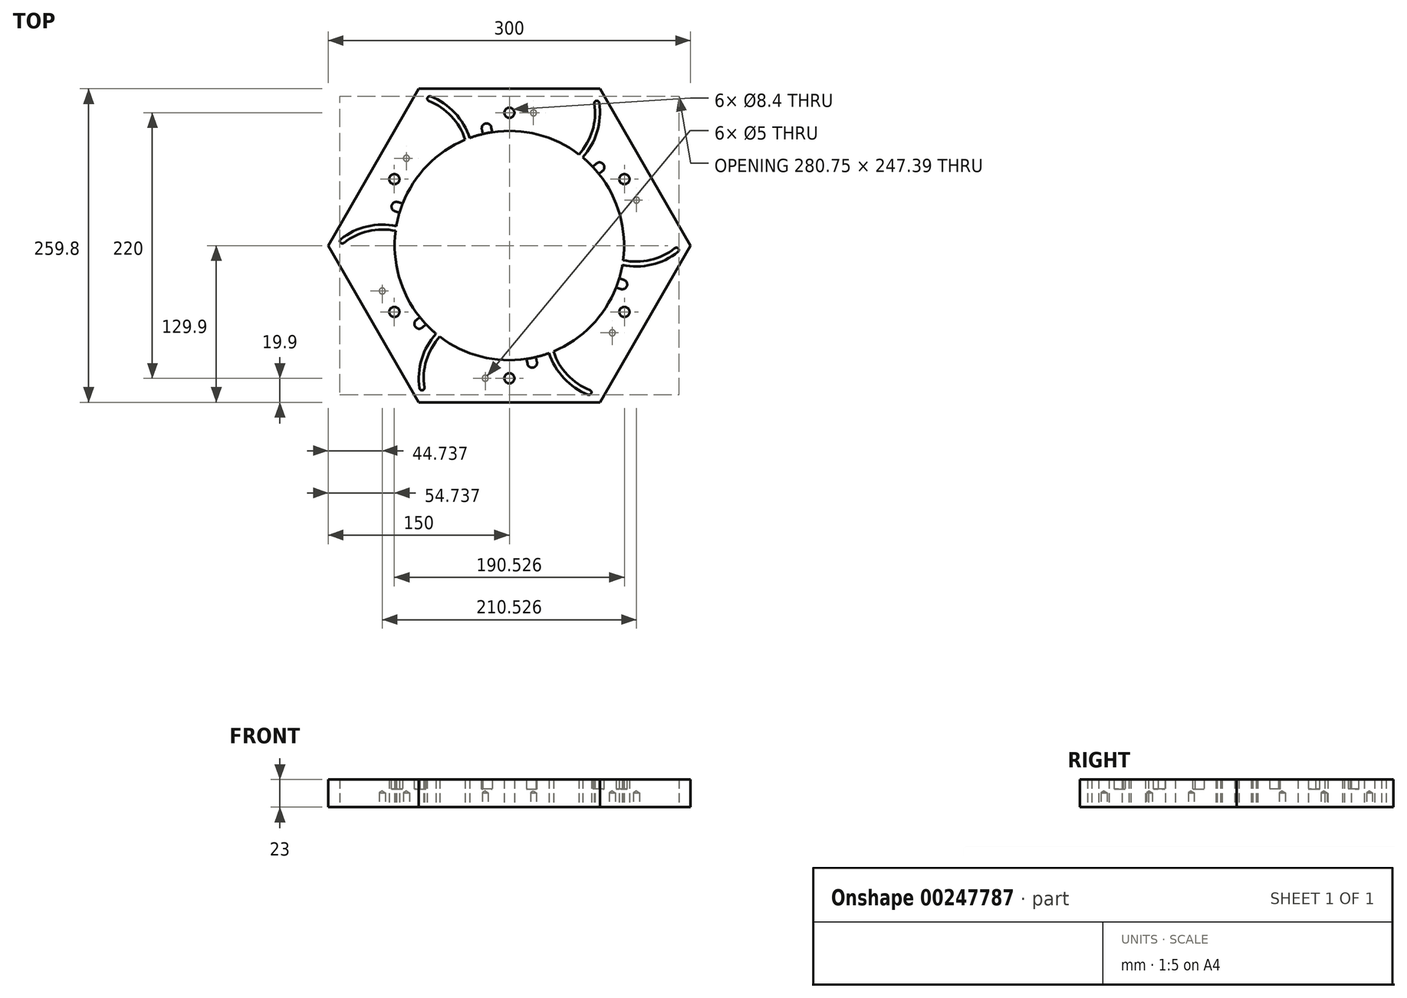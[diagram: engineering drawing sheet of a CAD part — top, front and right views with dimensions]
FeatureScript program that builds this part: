
annotation { "Feature Type Name" : "Feature", "Feature Type Description" : "" }
export const myFeature = defineFeature(function(context is Context, id is Id, definition is map)
    precondition{}
    {
        {
            var Q0;
            Q0=qCreatedBy(makeId("Top.planeOp"),FACE);
            var sketch = newSketch(context, id + "F0", { "sketchPlane" : qUnion([Q0])});
            skCircle(sketch, "E0.cCircle", {"center": v(0, 0) * mm, "radius": 150 * mm, "construction": true});
            skLineSegment(sketch, "E0.0", {"start": v(-75, 129.9) * mm, "end": v(75, 129.9) * mm});
            skLineSegment(sketch, "E0.1", {"start": v(75, 129.9) * mm, "end": v(150, 0) * mm});
            skLineSegment(sketch, "E0.2", {"start": v(150, 0) * mm, "end": v(75, -129.9) * mm});
            skLineSegment(sketch, "E0.3", {"start": v(75, -129.9) * mm, "end": v(-75, -129.9) * mm});
            skLineSegment(sketch, "E0.4", {"start": v(-75, -129.9) * mm, "end": v(-150, 0) * mm});
            skLineSegment(sketch, "E0.5", {"start": v(-150, 0) * mm, "end": v(-75, 129.9) * mm});
            skCircle(sketch, "E1", {"center": v(0, 0) * mm, "radius": 95 * mm});
            skCircle(sketch, "E2", {"center": v(0, 0) * mm, "radius": 110 * mm, "construction": true});
            skCircle(sketch, "E3", {"center": v(0, 110) * mm, "radius": 4.2 * mm});
            skCircle(sketch, "E4.1.0", {"center": v(-95.26, 55) * mm, "radius": 4.2 * mm});
            skCircle(sketch, "E4.2.0", {"center": v(-95.26, -55) * mm, "radius": 4.2 * mm});
            skCircle(sketch, "E4.3.0", {"center": v(0, -110) * mm, "radius": 4.2 * mm});
            skCircle(sketch, "E4.4.0", {"center": v(95.26, -55) * mm, "radius": 4.2 * mm});
            skCircle(sketch, "E4.5.0", {"center": v(95.26, 55) * mm, "radius": 4.2 * mm});
            skSolve(sketch);
        }
        {
            var Q0;
            Q0=qCreatedBy(makeId("Front.planeOp"),FACE);
            var sketch = newSketch(context, id + "F1", { "sketchPlane" : qUnion([Q0])});
            skLineSegment(sketch, "E5", {"start": v(0, -93.36) * mm, "end": v(0, 93) * mm, "construction": true});
            skSolve(sketch);
        }
        {
            var Q0;
            Q0=makeQuery(id+"F0.imprint","IMPRINT",FACE,{"disambiguationData":[TD([[makeQuery(id+"F0.imprint","IMPRINT",EDGE,{"derivedFrom":sQuery(id+"F0.wireOp",EDGE,"E0.0")}),-1.0]])]});
            extrude(context, id + "F2", {"entities" : qUnion([Q0]), "depth" : 25 * mm, "hasSecondDirection" : true, "secondDirectionOppositeDirection" : false, "secondDirectionDepth" : 2 * mm});
        }
        {
            var Q0;
            Q0=qCreatedBy(makeId("Top.planeOp"),FACE);
            var sketch = newSketch(context, id + "F3", { "sketchPlane" : qUnion([Q0])});
            skArc(sketch, "E6.0", {"start": v(-30.7, 79.26) * mm, "mid": v(-41.9, 106.16) * mm, "end": v(-65.27, 123.56) * mm});
            skArc(sketch, "E7.0", {"start": v(-34.54, 77.66) * mm, "mid": v(-44.72, 103.26) * mm, "end": v(-66.72, 119.83) * mm});
            skArc(sketch, "E8.0", {"start": v(-67.73, 122.7) * mm, "mid": v(-67.88, 121.03) * mm, "end": v(-66.72, 119.83) * mm});
            skArc(sketch, "E9.0", {"start": v(-65.27, 123.56) * mm, "mid": v(-66.66, 123.58) * mm, "end": v(-67.73, 122.7) * mm});
            skArc(sketch, "E10.0", {"start": v(-30.7, 79.26) * mm, "mid": v(-32.63, 78.49) * mm, "end": v(-34.54, 77.66) * mm});
            skSolve(sketch);
        }
        {
            var Q0;
            Q0=qSketchRegion(id+"F3",true);
            extrude(context, id + "F4", {"entities" : qUnion([Q0]), "depth" : 35 * mm, "hasSecondDirection" : true, "secondDirectionOppositeDirection" : true, "secondDirectionDepth" : 10 * mm});
        }
        {
            var Q0;
            Q0=makeQuery(id+"F4.opExtrude","SWEPT_BODY",BODY,{"disambiguationData":[OSD([sQuery(id+"F3.wireOp",EDGE,"E6.0"),sQuery(id+"F3.wireOp",EDGE,"E7.0"),sQuery(id+"F3.wireOp",EDGE,"E8.0"),sQuery(id+"F3.wireOp",EDGE,"E9.0"),sQuery(id+"F3.wireOp",EDGE,"E10.0")])]});
            var Q1;
            Q1=sQuery(id+"F1.wireOp",EDGE,"E5");
            circularPattern(context, id + "F5", {"entities" : qUnion([Q0]), "axis" : qUnion([Q1]), "angle" : 360 * degree, "instanceCount" : 6, "equalSpace" : true});
        }
        {
            var Q0;
            Q0=makeQuery(id+"F4.opExtrude","SWEPT_BODY",BODY,{"disambiguationData":[OSD([sQuery(id+"F3.wireOp",EDGE,"E6.0"),sQuery(id+"F3.wireOp",EDGE,"E7.0"),sQuery(id+"F3.wireOp",EDGE,"E8.0"),sQuery(id+"F3.wireOp",EDGE,"E9.0"),sQuery(id+"F3.wireOp",EDGE,"E10.0")])]});
            var Q1;
            Q1=makeQuery(id+"F5.opPattern","COPY",BODY,{"derivedFrom":makeQuery(id+"F4.opExtrude","SWEPT_BODY",BODY,{"disambiguationData":[OSD([sQuery(id+"F3.wireOp",EDGE,"E6.0"),sQuery(id+"F3.wireOp",EDGE,"E7.0"),sQuery(id+"F3.wireOp",EDGE,"E8.0"),sQuery(id+"F3.wireOp",EDGE,"E9.0"),sQuery(id+"F3.wireOp",EDGE,"E10.0")])]}),"instanceName":"5"});
            var Q2;
            Q2=makeQuery(id+"F5.opPattern","COPY",BODY,{"derivedFrom":makeQuery(id+"F4.opExtrude","SWEPT_BODY",BODY,{"disambiguationData":[OSD([sQuery(id+"F3.wireOp",EDGE,"E6.0"),sQuery(id+"F3.wireOp",EDGE,"E7.0"),sQuery(id+"F3.wireOp",EDGE,"E8.0"),sQuery(id+"F3.wireOp",EDGE,"E9.0"),sQuery(id+"F3.wireOp",EDGE,"E10.0")])]}),"instanceName":"4"});
            var Q3;
            Q3=makeQuery(id+"F5.opPattern","COPY",BODY,{"derivedFrom":makeQuery(id+"F4.opExtrude","SWEPT_BODY",BODY,{"disambiguationData":[OSD([sQuery(id+"F3.wireOp",EDGE,"E6.0"),sQuery(id+"F3.wireOp",EDGE,"E7.0"),sQuery(id+"F3.wireOp",EDGE,"E8.0"),sQuery(id+"F3.wireOp",EDGE,"E9.0"),sQuery(id+"F3.wireOp",EDGE,"E10.0")])]}),"instanceName":"3"});
            var Q4;
            Q4=makeQuery(id+"F5.opPattern","COPY",BODY,{"derivedFrom":makeQuery(id+"F4.opExtrude","SWEPT_BODY",BODY,{"disambiguationData":[OSD([sQuery(id+"F3.wireOp",EDGE,"E6.0"),sQuery(id+"F3.wireOp",EDGE,"E7.0"),sQuery(id+"F3.wireOp",EDGE,"E8.0"),sQuery(id+"F3.wireOp",EDGE,"E9.0"),sQuery(id+"F3.wireOp",EDGE,"E10.0")])]}),"instanceName":"2"});
            var Q5;
            Q5=makeQuery(id+"F5.opPattern","COPY",BODY,{"derivedFrom":makeQuery(id+"F4.opExtrude","SWEPT_BODY",BODY,{"disambiguationData":[OSD([sQuery(id+"F3.wireOp",EDGE,"E6.0"),sQuery(id+"F3.wireOp",EDGE,"E7.0"),sQuery(id+"F3.wireOp",EDGE,"E8.0"),sQuery(id+"F3.wireOp",EDGE,"E9.0"),sQuery(id+"F3.wireOp",EDGE,"E10.0")])]}),"instanceName":"1"});
            var Q6;
            Q6=makeQuery(id+"F2.opExtrude","SWEPT_BODY",BODY,{"disambiguationData":[OSD([sQuery(id+"F0.wireOp",EDGE,"E0.0"),sQuery(id+"F0.wireOp",EDGE,"E0.1"),sQuery(id+"F0.wireOp",EDGE,"E0.2"),sQuery(id+"F0.wireOp",EDGE,"E0.3"),sQuery(id+"F0.wireOp",EDGE,"E0.4"),sQuery(id+"F0.wireOp",EDGE,"E0.5"),sQuery(id+"F0.wireOp",EDGE,"E1")])]});
            booleanBodies(context, id + "F6", {"operationType" : BooleanOperationType.SUBTRACTION, "tools" : qUnion([Q0, Q1, Q2, Q3, Q4, Q5]), "targets" : qUnion([Q6])});
        }
        {
            var Q0;
            Q0=makeQuery(id+"F2.opExtrude","CAP_FACE",FACE,{"disambiguationData":[OSD([sQuery(id+"F0.wireOp",EDGE,"E0.0"),sQuery(id+"F0.wireOp",EDGE,"E0.1"),sQuery(id+"F0.wireOp",EDGE,"E0.2"),sQuery(id+"F0.wireOp",EDGE,"E0.3"),sQuery(id+"F0.wireOp",EDGE,"E0.4"),sQuery(id+"F0.wireOp",EDGE,"E0.5"),sQuery(id+"F0.wireOp",EDGE,"E1")])],"isStart":false});
            var sketch = newSketch(context, id + "F7", { "sketchPlane" : qUnion([Q0])});
            skCircle(sketch, "E11", {"center": v(0, 0) * mm, "radius": 95 * mm, "construction": true});
            skCircle(sketch, "E12", {"center": v(0, 0) * mm, "radius": 99 * mm, "construction": true});
            skLineSegment(sketch, "E13", {"start": v(0, 0) * mm, "end": v(0, 115.62) * mm, "construction": true});
            skLineSegment(sketch, "E14", {"start": v(0, 0) * mm, "end": v(-23.06, 118.63) * mm, "construction": true});
            skPoint(sketch, "E15", {"position": v(-18.9, 97.18) * mm});
            skArc(sketch, "E16", {"start": v(-19.65, 101.1) * mm, "mid": v(-22.23, 99.38) * mm, "end": v(-22.8, 96.34) * mm});
            skLineSegment(sketch, "E17", {"start": v(-22.82, 96.42) * mm, "end": v(-20.7, 85.51) * mm});
            skLineSegment(sketch, "E18", {"start": v(-16.77, 86.28) * mm, "end": v(-20.7, 85.51) * mm});
            skArc(sketch, "E19.MirrorCS", {"start": v(-19.65, 101.1) * mm, "mid": v(-16.62, 100.47) * mm, "end": v(-14.95, 97.86) * mm});
            skLineSegment(sketch, "E20.MirrorCS", {"start": v(-16.77, 86.28) * mm, "end": v(-12.84, 87.04) * mm});
            skLineSegment(sketch, "E21.MirrorCS", {"start": v(-14.96, 97.94) * mm, "end": v(-12.84, 87.04) * mm});
            skSolve(sketch);
        }
        {
            var Q0;
            Q0=qSketchRegion(id+"F7",true);
            extrude(context, id + "F8", {"entities" : qUnion([Q0]), "oppositeDirection" : true, "depth" : 8 * mm, "hasSecondDirection" : true, "secondDirectionOppositeDirection" : false, "secondDirectionDepth" : 10 * mm});
        }
        {
            var Q0;
            Q0=makeQuery(id+"F8.opExtrude","SWEPT_BODY",BODY,{"disambiguationData":[OSD([sQuery(id+"F7.wireOp",EDGE,"E16"),sQuery(id+"F7.wireOp",EDGE,"E17"),sQuery(id+"F7.wireOp",EDGE,"E18"),sQuery(id+"F7.wireOp",EDGE,"E19.MirrorCS"),sQuery(id+"F7.wireOp",EDGE,"E20.MirrorCS"),sQuery(id+"F7.wireOp",EDGE,"E21.MirrorCS")])]});
            var Q1;
            Q1=sQuery(id+"F1.wireOp",EDGE,"E5");
            circularPattern(context, id + "F9", {"operationType" : NewBodyOperationType.REMOVE, "entities" : qUnion([Q0]), "axis" : qUnion([Q1]), "angle" : 360 * degree, "instanceCount" : 6, "equalSpace" : true});
        }
        {
            var Q0;
            Q0=makeQuery(id+"F0.imprint","IMPRINT",FACE,{"disambiguationData":[TD([[makeQuery(id+"F0.imprint","IMPRINT",EDGE,{"derivedFrom":sQuery(id+"F0.wireOp",EDGE,"E0.0")}),-1.0]])]});
            cPlane(context, id + "F10", {"entities" : qUnion([Q0]), "cplaneType" : CPlaneType.OFFSET, "offset" : 0 * mm, "width" : 150 * mm, "height" : 150 * mm});
        }
        {
            var Q0;
            Q0=qCreatedBy(id+"F10.planeOp",FACE);
            var sketch = newSketch(context, id + "F11", { "sketchPlane" : qUnion([Q0])});
            skPoint(sketch, "E22.0", {"position": v(-85.26, 72.32) * mm});
            skPoint(sketch, "E23.1.0", {"position": v(-105.26, -37.68) * mm});
            skPoint(sketch, "E23.2.0", {"position": v(-20, -110) * mm});
            skPoint(sketch, "E23.3.0", {"position": v(85.26, -72.32) * mm});
            skPoint(sketch, "E23.4.0", {"position": v(105.26, 37.68) * mm});
            skPoint(sketch, "E23.5.0", {"position": v(20, 110) * mm});
            skPoint(sketch, "E23.center", {"position": v(0, 0) * mm});
            skSolve(sketch);
        }
        {
            var Q0;
            Q0=sQuery(id+"F11.wireOp",VERTEX,"E22.0");
            var Q1;
            Q1=sQuery(id+"F11.wireOp",VERTEX,"E23.5.0");
            var Q2;
            Q2=sQuery(id+"F11.wireOp",VERTEX,"E23.4.0");
            var Q3;
            Q3=sQuery(id+"F11.wireOp",VERTEX,"E23.3.0");
            var Q4;
            Q4=sQuery(id+"F11.wireOp",VERTEX,"E23.2.0");
            var Q5;
            Q5=sQuery(id+"F11.wireOp",VERTEX,"E23.1.0");
            var Q6;
            Q6=makeQuery(id+"F2.opExtrude","SWEPT_BODY",BODY,{"disambiguationData":[OSD([sQuery(id+"F0.wireOp",EDGE,"E0.0"),sQuery(id+"F0.wireOp",EDGE,"E0.1"),sQuery(id+"F0.wireOp",EDGE,"E0.2"),sQuery(id+"F0.wireOp",EDGE,"E0.3"),sQuery(id+"F0.wireOp",EDGE,"E0.4"),sQuery(id+"F0.wireOp",EDGE,"E0.5"),sQuery(id+"F0.wireOp",EDGE,"E1"),sQuery(id+"F0.wireOp",EDGE,"E3"),sQuery(id+"F0.wireOp",EDGE,"E4.1.0"),sQuery(id+"F0.wireOp",EDGE,"E4.2.0"),sQuery(id+"F0.wireOp",EDGE,"E4.3.0"),sQuery(id+"F0.wireOp",EDGE,"E4.4.0"),sQuery(id+"F0.wireOp",EDGE,"E4.5.0")])]});
            hole(context, id + "F12", {"style" : HoleStyle.SIMPLE, "endStyle" : HoleEndStyle.BLIND, "oppositeDirection" : true, "holeDiameter" : 5 * mm, "holeDepth" : 12 * mm, "locations" : qUnion([Q0, Q1, Q2, Q3, Q4, Q5]), "scope" : qUnion([Q6])});
        }
    });
